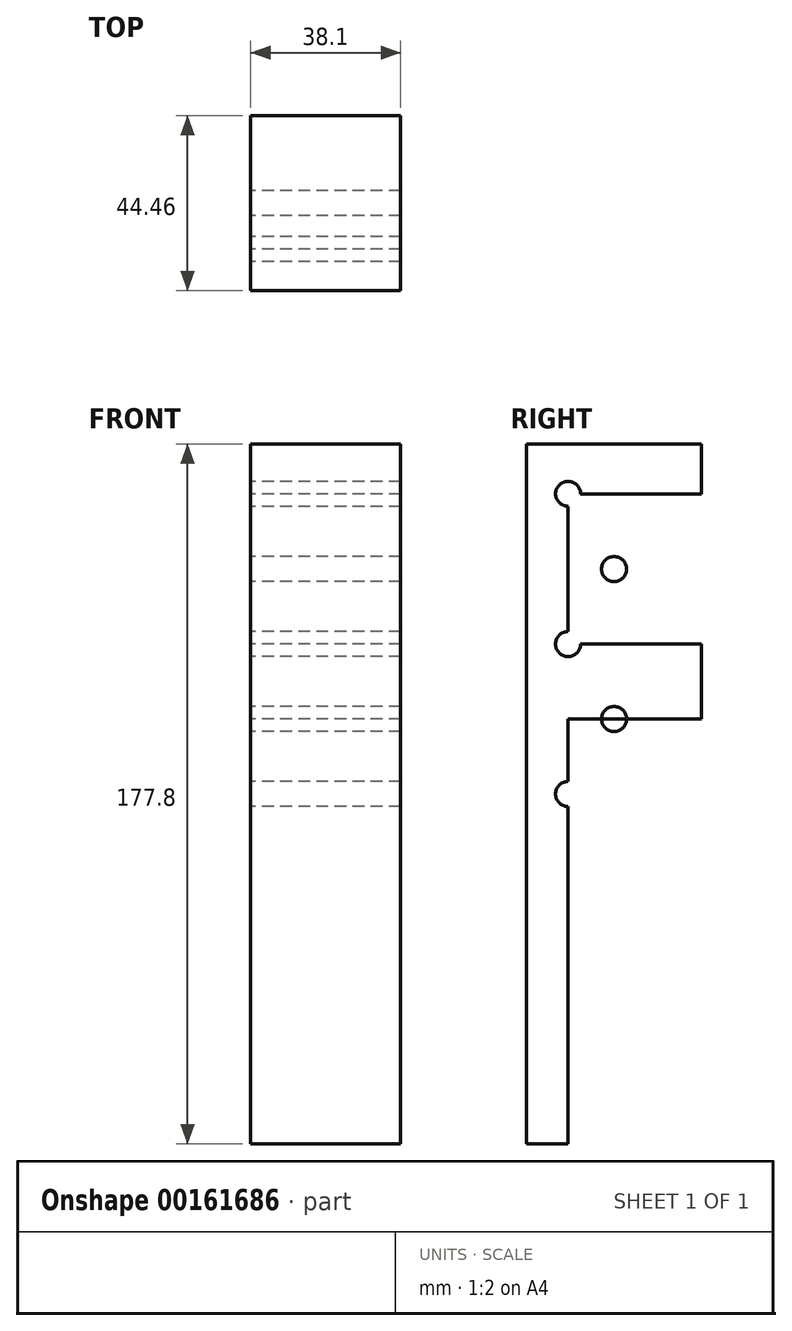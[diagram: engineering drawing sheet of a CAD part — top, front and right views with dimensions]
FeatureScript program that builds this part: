
annotation { "Feature Type Name" : "Feature", "Feature Type Description" : "" }
export const myFeature = defineFeature(function(context is Context, id is Id, definition is map)
    precondition{}
    {
        {
            var Q0;
            Q0=qCreatedBy(makeId("Right.planeOp"),FACE);
            var sketch = newSketch(context, id + "F0", { "sketchPlane" : qUnion([Q0])});
            skLineSegment(sketch, "E0.bottom", {"start": v(-22.22, 88.9) * mm, "end": v(22.23, 88.9) * mm});
            skLineSegment(sketch, "E0.top", {"start": v(-22.23, -88.9) * mm, "end": v(22.23, -88.9) * mm});
            skLineSegment(sketch, "E0.left", {"start": v(-22.22, 88.9) * mm, "end": v(-22.23, -88.9) * mm});
            skLineSegment(sketch, "E0.right", {"start": v(22.23, 88.9) * mm, "end": v(22.22, -88.9) * mm});
            skPoint(sketch, "E0.middle", {"position": v(0, 0) * mm});
            skLineSegment(sketch, "E1", {"start": v(22.23, -88.9) * mm, "end": v(22.23, 19.05) * mm});
            skLineSegment(sketch, "E2", {"start": v(22.23, 19.05) * mm, "end": v(-22.22, 19.05) * mm});
            skCircle(sketch, "E3", {"center": v(0, 19.05) * mm, "radius": 3.18 * mm});
            skLineSegment(sketch, "E4", {"start": v(22.23, -88.9) * mm, "end": v(22.23, -19.05) * mm});
            skLineSegment(sketch, "E5", {"start": v(22.23, -19.05) * mm, "end": v(-22.22, -19.05) * mm});
            skCircle(sketch, "E6", {"center": v(0, -19.05) * mm, "radius": 3.18 * mm});
            skLineSegment(sketch, "E7", {"start": v(22.23, -88.9) * mm, "end": v(22.23, 57.15) * mm});
            skLineSegment(sketch, "E8", {"start": v(22.23, 57.15) * mm, "end": v(-22.22, 57.15) * mm});
            skCircle(sketch, "E9", {"center": v(0, 57.15) * mm, "radius": 3.18 * mm});
            skLineSegment(sketch, "E10", {"start": v(-22.22, 76.28) * mm, "end": v(22.23, 76.28) * mm});
            skCircle(sketch, "E11", {"center": v(-11.67, 76.28) * mm, "radius": 3.18 * mm});
            skLineSegment(sketch, "E12", {"start": v(-22.22, 38.1) * mm, "end": v(22.23, 38.1) * mm});
            skLineSegment(sketch, "E13", {"start": v(-11.67, 76.28) * mm, "end": v(-11.67, -91.52) * mm});
            skCircle(sketch, "E14", {"center": v(-11.67, 38.1) * mm, "radius": 3.18 * mm});
            skCircle(sketch, "E15", {"center": v(-11.67, 0) * mm, "radius": 3.18 * mm});
            skSolve(sketch);
        }
        {
            var Q0;
            {var subQ8=sQuery(id+"F0.wireOp",EDGE,"E0.top");Q0=makeQuery(id+"F0.imprint","IMPRINT",FACE,{"disambiguationData":[TD([[makeQuery(id+"F0.imprint","IMPRINT",EDGE,{"derivedFrom":subQ8}),1.0]])]});}
            var Q1;
            {var subQ1=sQuery(id+"F0.wireOp",EDGE,"E2");var subQ4=sQuery(id+"F0.wireOp",EDGE,"E0.left");var subQ5=makeQuery(id+"F0.imprint","INTERSECT",VERTEX,{"derivedFrom":[subQ4,subQ1]});Q1=makeQuery(id+"F0.imprint","IMPRINT",FACE,{"disambiguationData":[TD([[makeQuery(id+"F0.imprint","IMPRINT",EDGE,{"disambiguationData":[TD([[subQ5,1.0]])],"derivedFrom":subQ4}),1.0]])]});}
            var Q2;
            {var subQ1=sQuery(id+"F0.wireOp",EDGE,"E2");var subQ4=sQuery(id+"F0.wireOp",EDGE,"E0.left");var subQ5=makeQuery(id+"F0.imprint","INTERSECT",VERTEX,{"derivedFrom":[subQ4,subQ1]});Q2=makeQuery(id+"F0.imprint","IMPRINT",FACE,{"disambiguationData":[TD([[makeQuery(id+"F0.imprint","IMPRINT",EDGE,{"disambiguationData":[TD([[subQ5,-1.0]])],"derivedFrom":subQ4}),1.0]])]});}
            var Q3;
            {var subQ4=sQuery(id+"F0.wireOp",EDGE,"E0.bottom");Q3=makeQuery(id+"F0.imprint","IMPRINT",FACE,{"disambiguationData":[TD([[makeQuery(id+"F0.imprint","IMPRINT",EDGE,{"derivedFrom":subQ4}),-1.0]])]});}
            var Q4;
            {var subQ1=sQuery(id+"F0.wireOp",EDGE,"E2");var subQ8=sQuery(id+"F0.wireOp",EDGE,"E7");var subQ9=makeQuery(id+"F0.imprint","INTERSECT",VERTEX,{"derivedFrom":[subQ1,subQ8]});Q4=makeQuery(id+"F0.imprint","IMPRINT",FACE,{"disambiguationData":[TD([[makeQuery(id+"F0.imprint","IMPRINT",EDGE,{"disambiguationData":[TD([[subQ9,-1.0]])],"derivedFrom":subQ1}),-1.0]])]});}
            var Q5;
            {var subQ0=sQuery(id+"F0.wireOp",EDGE,"E9");var subQ1=sQuery(id+"F0.wireOp",EDGE,"E8");var subQ3=makeQuery(id+"F0.imprint","INTERSECT",VERTEX,{"disambiguationData":[OD(1.0)],"derivedFrom":[subQ1,subQ0]});Q5=makeQuery(id+"F0.imprint","IMPRINT",FACE,{"disambiguationData":[TD([[makeQuery(id+"F0.imprint","IMPRINT",EDGE,{"disambiguationData":[TD([[subQ3,-1.0]])],"derivedFrom":subQ1}),-1.0]])]});}
            var Q6;
            {var subQ5=sQuery(id+"F0.wireOp",EDGE,"E0.left");var subQ7=sQuery(id+"F0.wireOp",EDGE,"E8");var subQ8=makeQuery(id+"F0.imprint","INTERSECT",VERTEX,{"derivedFrom":[subQ5,subQ7]});Q6=makeQuery(id+"F0.imprint","IMPRINT",FACE,{"disambiguationData":[TD([[makeQuery(id+"F0.imprint","IMPRINT",EDGE,{"disambiguationData":[TD([[subQ8,1.0]])],"derivedFrom":subQ5}),1.0]])]});}
            var Q7;
            {var subQ1=sQuery(id+"F0.wireOp",EDGE,"E8");var subQ6=sQuery(id+"F0.wireOp",EDGE,"E0.left");var subQ9=makeQuery(id+"F0.imprint","INTERSECT",VERTEX,{"derivedFrom":[subQ6,subQ1]});Q7=makeQuery(id+"F0.imprint","IMPRINT",FACE,{"disambiguationData":[TD([[makeQuery(id+"F0.imprint","IMPRINT",EDGE,{"disambiguationData":[TD([[subQ9,-1.0]])],"derivedFrom":subQ6}),1.0]])]});}
            var Q8;
            {var subQ0=sQuery(id+"F0.wireOp",EDGE,"E9");var subQ1=sQuery(id+"F0.wireOp",EDGE,"E8");var subQ3=makeQuery(id+"F0.imprint","INTERSECT",VERTEX,{"disambiguationData":[OD(1.0)],"derivedFrom":[subQ1,subQ0]});Q8=makeQuery(id+"F0.imprint","IMPRINT",FACE,{"disambiguationData":[TD([[makeQuery(id+"F0.imprint","IMPRINT",EDGE,{"disambiguationData":[TD([[subQ3,-1.0]])],"derivedFrom":subQ1}),1.0]])]});}
            var Q9;
            {var subQ0=sQuery(id+"F0.wireOp",EDGE,"E7");var subQ6=sQuery(id+"F0.wireOp",EDGE,"E2");var subQ10=makeQuery(id+"F0.imprint","INTERSECT",VERTEX,{"derivedFrom":[subQ6,subQ0]});Q9=makeQuery(id+"F0.imprint","IMPRINT",FACE,{"disambiguationData":[TD([[makeQuery(id+"F0.imprint","IMPRINT",EDGE,{"disambiguationData":[TD([[subQ10,-1.0]])],"derivedFrom":subQ6}),1.0]])]});}
            var Q10;
            {var subQ4=sQuery(id+"F0.wireOp",EDGE,"E7");var subQ5=sQuery(id+"F0.wireOp",EDGE,"E0.top");var subQ6=makeQuery(id+"F0.imprint","INTERSECT",VERTEX,{"derivedFrom":[subQ5,subQ4]});Q10=makeQuery(id+"F0.imprint","IMPRINT",FACE,{"disambiguationData":[TD([[makeQuery(id+"F0.imprint","IMPRINT",EDGE,{"disambiguationData":[TD([[subQ6,1.0]])],"derivedFrom":subQ5}),1.0]])]});}
            extrude(context, id + "F1", {"entities" : qUnion([Q0, Q1, Q2, Q3, Q4, Q5, Q6, Q7, Q8, Q9, Q10]), "depth" : 38.1 * mm});
        }
    });
